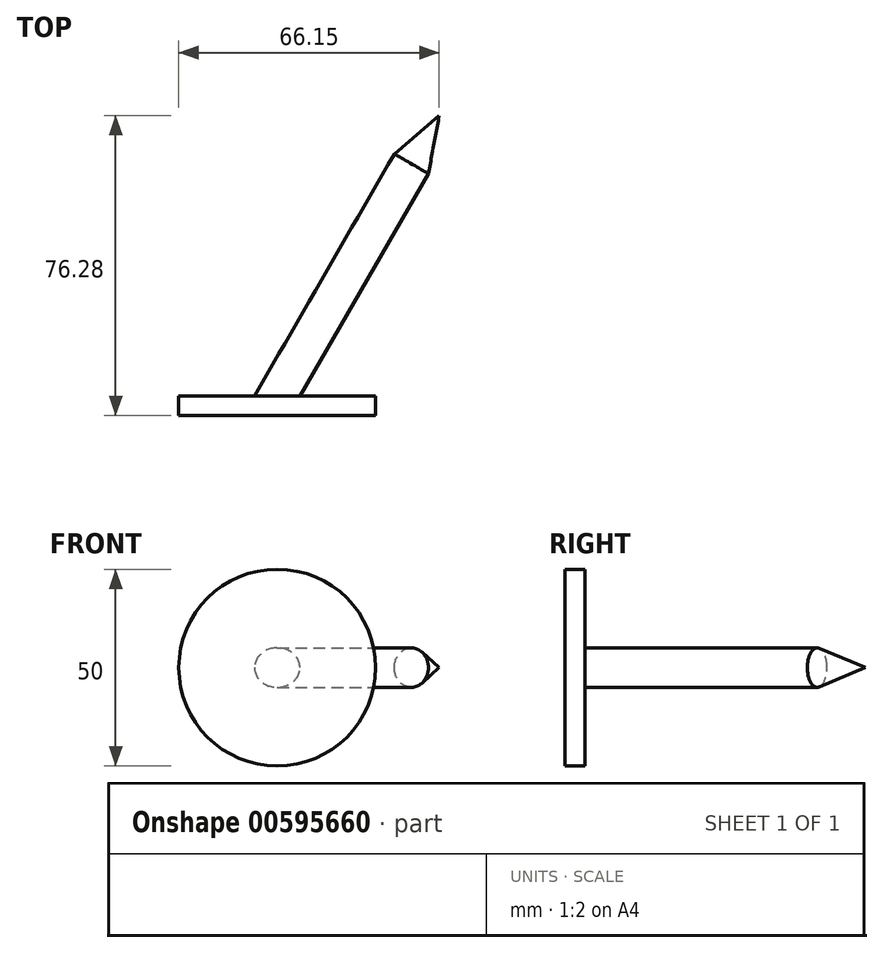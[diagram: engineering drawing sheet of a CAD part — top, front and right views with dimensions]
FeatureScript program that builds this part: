
annotation { "Feature Type Name" : "Feature", "Feature Type Description" : "" }
export const myFeature = defineFeature(function(context is Context, id is Id, definition is map)
    precondition{}
    {
        {
            var Q0;
            Q0=qCreatedBy(makeId("Top.planeOp"),FACE);
            var sketch = newSketch(context, id + "F0", { "sketchPlane" : qUnion([Q0])});
            skLineSegment(sketch, "E0", {"start": v(0, 0) * mm, "end": v(25, 0) * mm});
            skLineSegment(sketch, "E1", {"start": v(0, 0) * mm, "end": v(0, 60) * mm, "construction": true});
            skLineSegment(sketch, "E2.0", {"start": v(0, -5) * mm, "end": v(25, -5) * mm});
            skLineSegment(sketch, "E3", {"start": v(25, 0) * mm, "end": v(25, -5) * mm});
            skLineSegment(sketch, "E4", {"start": v(0, 0) * mm, "end": v(0, -5) * mm});
            skLineSegment(sketch, "E5", {"start": v(41.15, 71.28) * mm, "end": v(-2.89, -5) * mm});
            skLineSegment(sketch, "E6", {"start": v(-2.89, -5) * mm, "end": v(2.89, -5) * mm});
            skLineSegment(sketch, "E7.0", {"start": v(38.41, 56.53) * mm, "end": v(2.89, -5) * mm});
            skLineSegment(sketch, "E8", {"start": v(41.15, 71.28) * mm, "end": v(38.41, 56.53) * mm});
            skSolve(sketch);
        }
        {
            var Q0;
            Q0=makeQuery(id+"F0.imprint","IMPRINT",FACE,{"disambiguationData":[TD([[makeQuery(id+"F0.imprint","IMPRINT",EDGE,{"derivedFrom":sQuery(id+"F0.wireOp",EDGE,"E2.0")}),1.0]])]});
            var Q1;
            {var subQ0=sQuery(id+"F0.wireOp",EDGE,"E4");Q1=makeQuery(id+"F0.imprint","IMPRINT",FACE,{"disambiguationData":[TD([[makeQuery(id+"F0.imprint","IMPRINT",EDGE,{"derivedFrom":subQ0}),1.0]])]});}
            var Q2;
            Q2=sQuery(id+"F0.wireOp",EDGE,"E1");
            revolve(context, id + "F1", {"entities" : qUnion([Q0, Q1]), "axis" : qUnion([Q2]), "revolveType" : RevolveType.FULL});
        }
        {
            var Q0;
            {var subQ5=sQuery(id+"F0.wireOp",EDGE,"E8");Q0=makeQuery(id+"F0.imprint","IMPRINT",FACE,{"disambiguationData":[TD([[makeQuery(id+"F0.imprint","IMPRINT",EDGE,{"derivedFrom":subQ5}),-1.0]])]});}
            var Q1;
            {var subQ0=sQuery(id+"F0.wireOp",EDGE,"E4");Q1=makeQuery(id+"F0.imprint","IMPRINT",FACE,{"disambiguationData":[TD([[makeQuery(id+"F0.imprint","IMPRINT",EDGE,{"derivedFrom":subQ0}),1.0]])]});}
            var Q2;
            {var subQ0=sQuery(id+"F0.wireOp",EDGE,"E4");Q2=makeQuery(id+"F0.imprint","IMPRINT",FACE,{"disambiguationData":[TD([[makeQuery(id+"F0.imprint","IMPRINT",EDGE,{"derivedFrom":subQ0}),-1.0]])]});}
            var Q3;
            Q3=sQuery(id+"F0.wireOp",EDGE,"E5");
            revolve(context, id + "F2", {"operationType" : NewBodyOperationType.ADD, "entities" : qUnion([Q0, Q1, Q2]), "axis" : qUnion([Q3]), "revolveType" : RevolveType.FULL});
        }
    });
